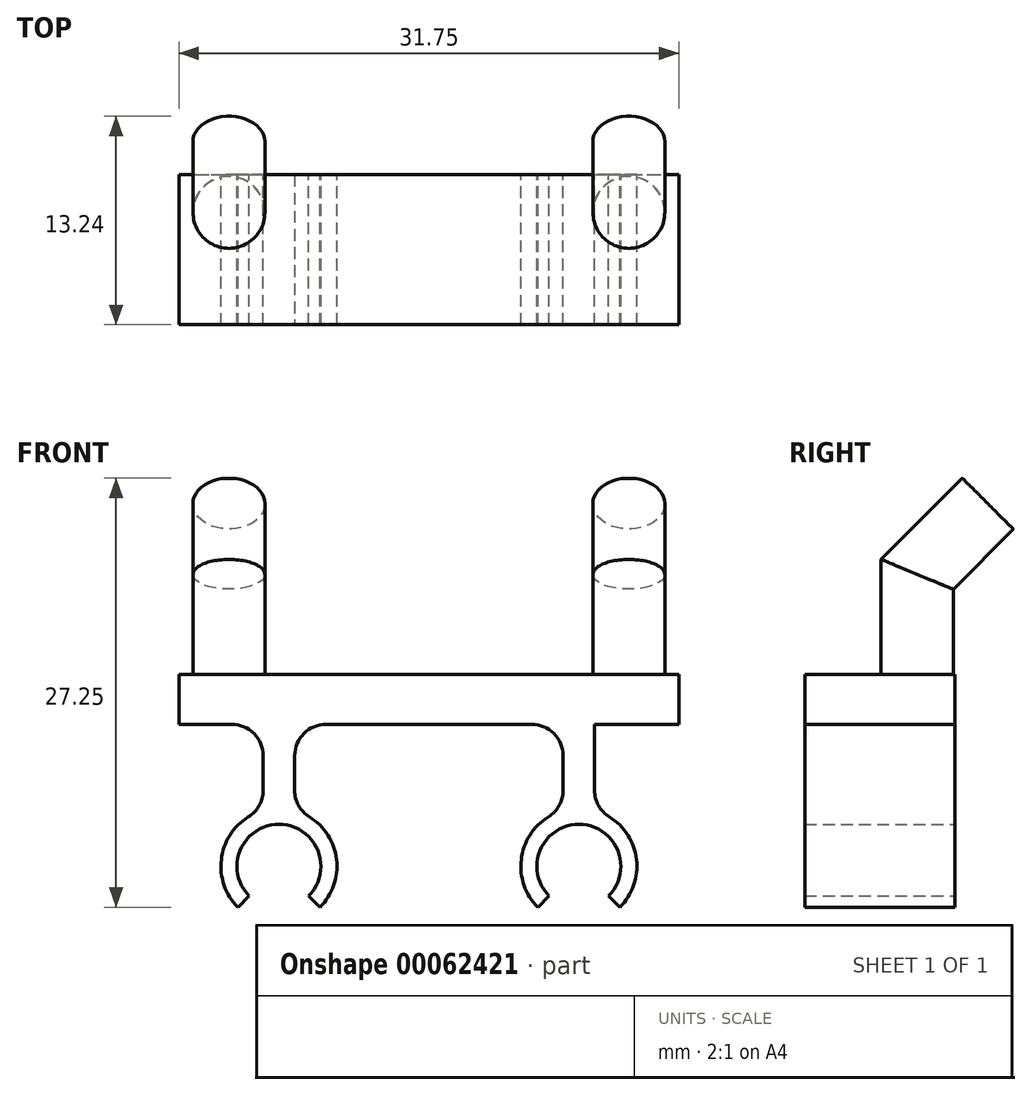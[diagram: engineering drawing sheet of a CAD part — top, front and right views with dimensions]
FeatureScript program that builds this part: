
annotation { "Feature Type Name" : "Feature", "Feature Type Description" : "" }
export const myFeature = defineFeature(function(context is Context, id is Id, definition is map)
    precondition{}
    {
        {
            var Q0;
            Q0=qCreatedBy(makeId("Top.planeOp"),FACE);
            var sketch = newSketch(context, id + "F0", { "sketchPlane" : qUnion([Q0])});
            skLineSegment(sketch, "E0.bottom", {"start": v(0, 0) * mm, "end": v(31.75, 0) * mm});
            skLineSegment(sketch, "E0.top", {"start": v(0, 9.52) * mm, "end": v(31.75, 9.52) * mm});
            skLineSegment(sketch, "E0.left", {"start": v(0, 0) * mm, "end": v(0, 9.52) * mm});
            skLineSegment(sketch, "E0.right", {"start": v(31.75, 0) * mm, "end": v(31.75, 9.52) * mm});
            skSolve(sketch);
        }
        {
            var Q0;
            Q0=makeQuery(id+"F0.imprint","IMPRINT",FACE,{"disambiguationData":[TD([[makeQuery(id+"F0.imprint","IMPRINT",EDGE,{"derivedFrom":sQuery(id+"F0.wireOp",EDGE,"E0.bottom")}),1.0]])]});
            extrude(context, id + "F1", {"entities" : qUnion([Q0]), "depth" : 3.17 * mm});
        }
        {
            var Q0;
            Q0=makeQuery(id+"F1.opExtrude","SWEPT_FACE",FACE,{"disambiguationData":[OSD([sQuery(id+"F0.wireOp",EDGE,"E0.right")])]});
            cPlane(context, id + "F2", {"entities" : qUnion([Q0]), "cplaneType" : CPlaneType.OFFSET, "offset" : 3.17 * mm, "oppositeDirection" : true, "width" : 152.4 * mm, "height" : 152.4 * mm});
        }
        {
            var Q0;
            Q0=qCreatedBy(id+"F2.planeOp",FACE);
            var sketch = newSketch(context, id + "F3", { "sketchPlane" : qUnion([Q0])});
            skLineSegment(sketch, "E1", {"start": v(7.14, 3.18) * mm, "end": v(7.14, 9.53) * mm});
            skLineSegment(sketch, "E2", {"start": v(7.14, 9.53) * mm, "end": v(11.63, 14.02) * mm});
            skSolve(sketch);
        }
        {
            var Q0;
            Q0=makeQuery(id+"F1.opExtrude","CAP_FACE",FACE,{"disambiguationData":[OSD([sQuery(id+"F0.wireOp",EDGE,"E0.bottom"),sQuery(id+"F0.wireOp",EDGE,"E0.top"),sQuery(id+"F0.wireOp",EDGE,"E0.left"),sQuery(id+"F0.wireOp",EDGE,"E0.right")])],"isStart":false});
            var sketch = newSketch(context, id + "F4", { "sketchPlane" : qUnion([Q0])});
            skCircle(sketch, "E3", {"center": v(28.57, 7.14) * mm, "radius": 2.29 * mm});
            skSolve(sketch);
        }
        {
            var Q0;
            Q0=makeQuery(id+"F4.imprint","IMPRINT",FACE,{"disambiguationData":[TD([[makeQuery(id+"F4.imprint","IMPRINT",EDGE,{"derivedFrom":sQuery(id+"F4.wireOp",EDGE,"E3")}),1.0]])]});
            var Q1;
            Q1=sQuery(id+"F3.wireOp",EDGE,"E1");
            var Q2;
            Q2=sQuery(id+"F3.wireOp",EDGE,"E2");
            sweep(context, id + "F5", {"operationType" : NewBodyOperationType.ADD, "profiles" : qUnion([Q0]), "path" : qUnion([Q1, Q2])});
        }
        {
            var Q0;
            Q0=qCreatedBy(id+"F2.planeOp",FACE);
            cPlane(context, id + "F6", {"entities" : qUnion([Q0]), "cplaneType" : CPlaneType.OFFSET, "offset" : 25.4 * mm, "oppositeDirection" : true, "width" : 152.4 * mm, "height" : 152.4 * mm});
        }
        {
            var Q0;
            Q0=qCreatedBy(id+"F6.planeOp",FACE);
            var sketch = newSketch(context, id + "F7", { "sketchPlane" : qUnion([Q0])});
            skLineSegment(sketch, "E4.0", {"start": v(7.14, 3.18) * mm, "end": v(7.14, 9.53) * mm});
            skLineSegment(sketch, "E4.1", {"start": v(7.14, 9.53) * mm, "end": v(11.63, 14.02) * mm});
            skSolve(sketch);
        }
        {
            var Q0;
            Q0=makeQuery(id+"F1.opExtrude","CAP_FACE",FACE,{"disambiguationData":[OSD([sQuery(id+"F0.wireOp",EDGE,"E0.bottom"),sQuery(id+"F0.wireOp",EDGE,"E0.top"),sQuery(id+"F0.wireOp",EDGE,"E0.left"),sQuery(id+"F0.wireOp",EDGE,"E0.right")])],"isStart":false});
            var sketch = newSketch(context, id + "F8", { "sketchPlane" : qUnion([Q0])});
            skCircle(sketch, "E5", {"center": v(3.17, 7.14) * mm, "radius": 2.29 * mm});
            skSolve(sketch);
        }
        {
            var Q0;
            Q0=makeQuery(id+"F8.imprint","IMPRINT",FACE,{"disambiguationData":[TD([[makeQuery(id+"F8.imprint","IMPRINT",EDGE,{"derivedFrom":sQuery(id+"F8.wireOp",EDGE,"E5")}),1.0]])]});
            var Q1;
            Q1=sQuery(id+"F7.wireOp",EDGE,"E4.0");
            var Q2;
            Q2=sQuery(id+"F7.wireOp",EDGE,"E4.1");
            sweep(context, id + "F9", {"operationType" : NewBodyOperationType.ADD, "profiles" : qUnion([Q0]), "path" : qUnion([Q1, Q2])});
        }
        {
            var Q0;
            Q0=makeQuery(id+"F1.opExtrude","SWEPT_FACE",FACE,{"disambiguationData":[OSD([sQuery(id+"F0.wireOp",EDGE,"E0.top")])]});
            var sketch = newSketch(context, id + "F10", { "sketchPlane" : qUnion([Q0])});
            skArc(sketch, "E6", {"start": v(-23.51, -10.9) * mm, "mid": v(-25.4, -6.35) * mm, "end": v(-27.29, -10.9) * mm});
            skArc(sketch, "E7", {"start": v(-4.46, -10.9) * mm, "mid": v(-6.35, -6.35) * mm, "end": v(-8.24, -10.9) * mm});
            skArc(sketch, "E8", {"start": v(-26.4, -5.47) * mm, "mid": v(-28.96, -8.09) * mm, "end": v(-28, -11.62) * mm});
            skArc(sketch, "E9", {"start": v(-7.35, -5.47) * mm, "mid": v(-9.91, -8.09) * mm, "end": v(-8.95, -11.62) * mm});
            skLineSegment(sketch, "E10.bottom", {"start": v(-5.35, 0) * mm, "end": v(-7.35, 0) * mm});
            skLineSegment(sketch, "E10.left", {"start": v(-5.35, 0) * mm, "end": v(-5.35, -5.47) * mm});
            skLineSegment(sketch, "E10.right", {"start": v(-7.35, 0) * mm, "end": v(-7.35, -5.47) * mm});
            skPoint(sketch, "E10.middle", {"position": v(-6.35, -2.74) * mm});
            skLineSegment(sketch, "E11.bottom", {"start": v(-24.4, 0) * mm, "end": v(-26.4, 0) * mm});
            skLineSegment(sketch, "E11.left", {"start": v(-24.4, 0) * mm, "end": v(-24.4, -5.47) * mm});
            skLineSegment(sketch, "E11.right", {"start": v(-26.4, 0) * mm, "end": v(-26.4, -5.47) * mm});
            skPoint(sketch, "E11.middle", {"position": v(-25.4, -2.74) * mm});
            skLineSegment(sketch, "E12", {"start": v(-27.29, -10.9) * mm, "end": v(-28, -11.62) * mm});
            skLineSegment(sketch, "E13", {"start": v(-23.51, -10.9) * mm, "end": v(-22.8, -11.62) * mm});
            skLineSegment(sketch, "E14", {"start": v(-8.24, -10.9) * mm, "end": v(-8.95, -11.62) * mm});
            skLineSegment(sketch, "E15", {"start": v(-4.46, -10.9) * mm, "end": v(-3.75, -11.62) * mm});
            skArc(sketch, "E16.trimOffspring", {"start": v(-22.8, -11.62) * mm, "mid": v(-21.84, -8.09) * mm, "end": v(-24.4, -5.47) * mm});
            skArc(sketch, "E17.trimOffspring", {"start": v(-3.75, -11.62) * mm, "mid": v(-2.79, -8.09) * mm, "end": v(-5.35, -5.47) * mm});
            skSolve(sketch);
        }
        {
            var Q0;
            Q0=makeQuery(id+"F10.imprint","IMPRINT",FACE,{"disambiguationData":[TD([[makeQuery(id+"F10.imprint","IMPRINT",EDGE,{"derivedFrom":sQuery(id+"F10.wireOp",EDGE,"E6")}),-1.0]])]});
            var Q1;
            Q1=makeQuery(id+"F10.imprint","IMPRINT",FACE,{"disambiguationData":[TD([[makeQuery(id+"F10.imprint","IMPRINT",EDGE,{"derivedFrom":sQuery(id+"F10.wireOp",EDGE,"E7")}),-1.0]])]});
            var Q2;
            Q2=makeQuery(id+"F1.opExtrude","SWEPT_FACE",FACE,{"disambiguationData":[OSD([sQuery(id+"F0.wireOp",EDGE,"E0.bottom")])]});
            extrude(context, id + "F11", {"entities" : qUnion([Q0, Q1]), "operationType" : NewBodyOperationType.ADD, "endBound" : BoundingType.UP_TO_SURFACE, "oppositeDirection" : true, "endBoundEntityFace" : qUnion([Q2]), "depth" : 25.4 * mm});
        }
        {
            var Q0;
            Q0=makeQuery(id+"F11.opExtrude","SWEPT_EDGE",EDGE,{"disambiguationData":[OSD([sQuery(id+"F0.wireOp",EDGE,"E0.top"),sQuery(id+"F10.wireOp",EDGE,"E11.bottom"),sQuery(id+"F10.wireOp",EDGE,"E11.right")])]});
            var Q1;
            Q1=makeQuery(id+"F11.opExtrude","SWEPT_EDGE",EDGE,{"disambiguationData":[OSD([sQuery(id+"F0.wireOp",EDGE,"E0.top"),sQuery(id+"F10.wireOp",EDGE,"E11.bottom"),sQuery(id+"F10.wireOp",EDGE,"E11.left")])]});
            var Q2;
            Q2=makeQuery(id+"F11.opExtrude","SWEPT_EDGE",EDGE,{"disambiguationData":[OSD([sQuery(id+"F0.wireOp",EDGE,"E0.top"),sQuery(id+"F10.wireOp",EDGE,"E10.bottom"),sQuery(id+"F10.wireOp",EDGE,"E10.right")])]});
            var Q3;
            Q3=makeQuery(id+"F11.opExtrude","SWEPT_EDGE",EDGE,{"disambiguationData":[OSD([sQuery(id+"F0.wireOp",EDGE,"E0.top"),sQuery(id+"F10.wireOp",EDGE,"E10.bottom"),sQuery(id+"F10.wireOp",EDGE,"E10.left")])]});
            var Q4;
            Q4=makeQuery(id+"F11.opExtrude","SWEPT_EDGE",EDGE,{"disambiguationData":[OSD([sQuery(id+"F10.wireOp",EDGE,"E11.left"),sQuery(id+"F10.wireOp",EDGE,"E16.trimOffspring")])]});
            var Q5;
            Q5=makeQuery(id+"F11.opExtrude","SWEPT_EDGE",EDGE,{"disambiguationData":[OSD([sQuery(id+"F10.wireOp",EDGE,"E8"),sQuery(id+"F10.wireOp",EDGE,"E11.right")])]});
            var Q6;
            Q6=makeQuery(id+"F11.opExtrude","SWEPT_EDGE",EDGE,{"disambiguationData":[OSD([sQuery(id+"F10.wireOp",EDGE,"E9"),sQuery(id+"F10.wireOp",EDGE,"E10.right")])]});
            var Q7;
            Q7=makeQuery(id+"F11.opExtrude","SWEPT_EDGE",EDGE,{"disambiguationData":[OSD([sQuery(id+"F10.wireOp",EDGE,"E10.left"),sQuery(id+"F10.wireOp",EDGE,"E17.trimOffspring")])]});
            fillet(context, id + "F12", {"entities" : qUnion([Q0, Q1, Q2, Q3, Q4, Q5, Q6, Q7]), "radius" : 2 * mm, "tangentPropagation" : true, "allowEdgeOverflow" : false});
        }
    });
